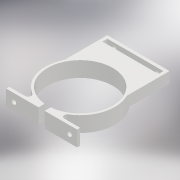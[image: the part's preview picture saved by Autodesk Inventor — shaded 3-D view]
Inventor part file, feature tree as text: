
AUTODESK INVENTOR PART (.ipt)
format: ipt  version: 2018.2 (Build 222227000, 227)  size: 184,320 bytes
history: native  units: mm
features: extrude x4, sketch x4, other x2, mirror x1, reference x1
ambient origin geometry x8: Origin, YZ Plane, XZ Plane, XY Plane, X Axis, Y Axis, Z Axis, Center Point
bodies: Solid1 (feature_tree)
feature tree (12):
  extrude  "Extrusion1"  Depth=25.0mm
  extrude  "Extrusion2"  Depth=2.0mm
  mirror  "Mirror1"
  extrude  "Extrusion3"  Depth=2.0mm
  extrude  "Extrusion4"  Depth=10.0mm TaperAngle=0.0deg
  sketch  "Sketch1"  dims[d1=25.0mm d2=36.0mm]
  sketch  "Sketch2"  dims[d3=2.0mm d4=1.4mm]
  sketch  "Sketch3"  dims[d5=5.0mm d6=2.0mm]
  reference  "Reference1"
  sketch  "Sketch4"  dims[d7=4.0mm d8=10.0mm d9=0.0mm d10=3.0mm d11=20.0mm d12=0.0mm d13=42.3mm d14=3.2mm d15=36.3mm d16=10.0mm d17=2.0mm d18=2.0mm d19=2.0mm d20=7.0mm d21=0.0mm d22=3.0mm d23=3.0mm d24=28.0mm d25=12.0mm d26=0.0mm]
  other  "PitchAssemblyOTS.iam"
  other  "OmegaRingTypeC:1"
